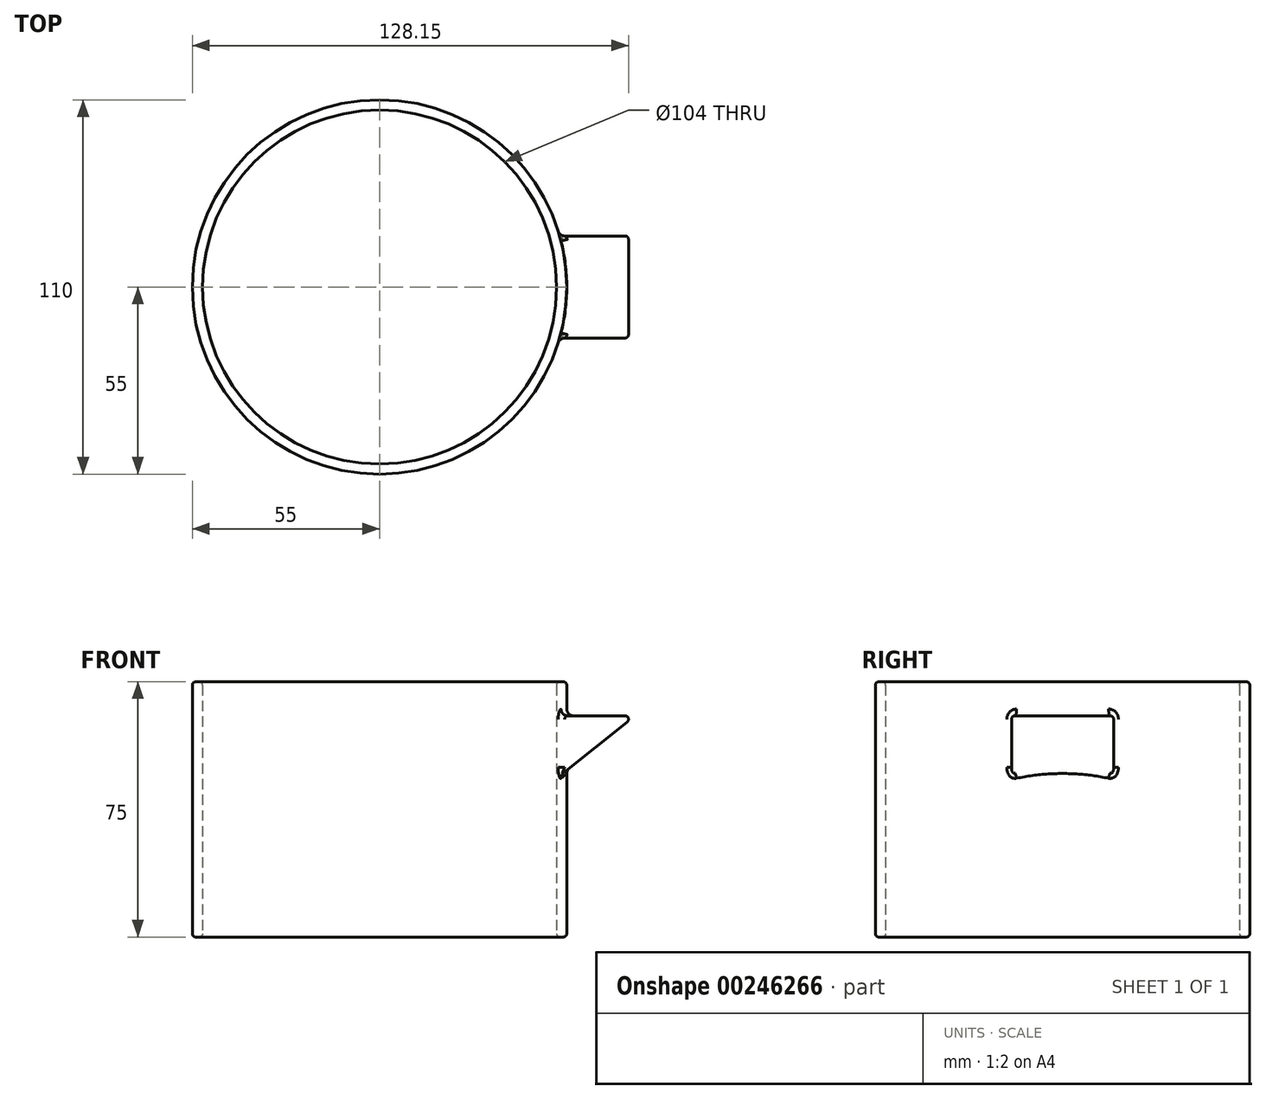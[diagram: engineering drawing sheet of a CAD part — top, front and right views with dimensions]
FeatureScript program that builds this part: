
annotation { "Feature Type Name" : "Feature", "Feature Type Description" : "" }
export const myFeature = defineFeature(function(context is Context, id is Id, definition is map)
    precondition{}
    {
        {
            var Q0;
            Q0=qCreatedBy(makeId("Top.planeOp"),FACE);
            var sketch = newSketch(context, id + "F0", { "sketchPlane" : qUnion([Q0])});
            skCircle(sketch, "E0", {"center": v(0, 0) * mm, "radius": 55 * mm});
            skCircle(sketch, "E1", {"center": v(0, 0) * mm, "radius": 52 * mm});
            skSolve(sketch);
        }
        {
            var Q0;
            Q0 = qSketchRegion(id + "F0", true);
            extrude(context, id + "F1", {"entities" : qUnion([Q0]), "depth" : 75 * mm});
        }
        {
            var Q0;
            Q0=qCreatedBy(makeId("Front.planeOp"),FACE);
            var sketch = newSketch(context, id + "F2", { "sketchPlane" : qUnion([Q0])});
            skLineSegment(sketch, "E2", {"start": v(50, 65) * mm, "end": v(75, 65) * mm});
            skLineSegment(sketch, "E3", {"start": v(75, 65) * mm, "end": v(50, 45) * mm});
            skLineSegment(sketch, "E4", {"start": v(50, 45) * mm, "end": v(50, 65) * mm});
            skSolve(sketch);
        }
        {
            var Q0;
            Q0 = qSketchRegion(id + "F2", true);
            extrude(context, id + "F3", {"entities" : qUnion([Q0]), "operationType" : NewBodyOperationType.ADD, "endBound" : BoundingType.SYMMETRIC, "depth" : 30 * mm});
        }
        {
            var Q0;
            Q0=makeQuery(id+"F1.opExtrude","CAP_FACE",FACE,{"disambiguationData":[OSD([sQuery(id+"F0.wireOp",EDGE,"E0"),sQuery(id+"F0.wireOp",EDGE,"E1")])],"isStart":false});
            var sketch = newSketch(context, id + "F4", { "sketchPlane" : qUnion([Q0])});
            skCircle(sketch, "E5.0", {"center": v(0, 0) * mm, "radius": 52 * mm});
            skSolve(sketch);
        }
        {
            var Q0;
            Q0 = qSketchRegion(id + "F4", true);
            extrude(context, id + "F5", {"entities" : qUnion([Q0]), "operationType" : NewBodyOperationType.REMOVE, "endBound" : BoundingType.THROUGH_ALL, "oppositeDirection" : true, "depth" : 25 * mm});
        }
        {
            var Q0;
            Q0=makeQuery(id+"F3.opExtrude","SWEPT_EDGE",EDGE,{"disambiguationData":[OSD([sQuery(id+"F2.wireOp",EDGE,"E2"),sQuery(id+"F2.wireOp",EDGE,"E3")])]});
            var Q1;
            Q1=makeQuery(id+"FyLVPSFapYQUoZB_1.1.F3.opExtrude","SWEPT_EDGE",EDGE,{"disambiguationData":[OSD([sQuery(id+"F2.wireOp",EDGE,"E2"),sQuery(id+"F2.wireOp",EDGE,"E3")])]});
            var Q2;
            Q2=makeQuery(id+"FyLVPSFapYQUoZB_1.1.F3.opExtrude","CAP_EDGE",EDGE,{"disambiguationData":[OSD([sQuery(id+"F2.wireOp",EDGE,"E3")])],"isStart":false});
            var Q3;
            Q3=makeQuery(id+"FyLVPSFapYQUoZB_1.1.F3.opExtrude","CAP_EDGE",EDGE,{"disambiguationData":[OSD([sQuery(id+"F2.wireOp",EDGE,"E2")])],"isStart":false});
            var Q4;
            Q4=makeQuery(id+"F3.opExtrude","CAP_EDGE",EDGE,{"disambiguationData":[OSD([sQuery(id+"F2.wireOp",EDGE,"E2")])],"isStart":false});
            var Q5;
            Q5=makeQuery(id+"F3.opExtrude","CAP_EDGE",EDGE,{"disambiguationData":[OSD([sQuery(id+"F2.wireOp",EDGE,"E3")])],"isStart":false});
            var Q6;
            Q6=makeQuery(id+"F3.opExtrude","CAP_EDGE",EDGE,{"disambiguationData":[OSD([sQuery(id+"F2.wireOp",EDGE,"E2")])],"isStart":true});
            var Q7;
            Q7=makeQuery(id+"F3.opExtrude","CAP_EDGE",EDGE,{"disambiguationData":[OSD([sQuery(id+"F2.wireOp",EDGE,"E3")])],"isStart":true});
            var Q8;
            Q8=makeQuery(id+"FyLVPSFapYQUoZB_1.1.F3.opExtrude","CAP_EDGE",EDGE,{"disambiguationData":[OSD([sQuery(id+"F2.wireOp",EDGE,"E3")])],"isStart":true});
            var Q9;
            Q9=makeQuery(id+"FyLVPSFapYQUoZB_1.1.F3.opExtrude","CAP_EDGE",EDGE,{"disambiguationData":[OSD([sQuery(id+"F2.wireOp",EDGE,"E2")])],"isStart":true});
            fillet(context, id + "F6", {"entities" : qUnion([Q0, Q1, Q2, Q3, Q4, Q5, Q6, Q7, Q8, Q9]), "radius" : 1 * mm, "tangentPropagation" : true, "allowEdgeOverflow" : false});
        }
        {
            var Q0;
            Q0=makeQuery(id+"F3.boolean.opBoolean","INTERSECT",EDGE,{"derivedFrom":[makeQuery(id+"F1.opExtrude","SWEPT_FACE",FACE,{"disambiguationData":[OSD([sQuery(id+"F0.wireOp",EDGE,"E0")])]}),makeQuery(id+"F3.opExtrude","SWEPT_FACE",FACE,{"disambiguationData":[OSD([sQuery(id+"F2.wireOp",EDGE,"E2")])]})]});
            var Q1;
            Q1=makeQuery(id+"FyLVPSFapYQUoZB_1.1.F3.boolean.opBoolean","INTERSECT",EDGE,{"derivedFrom":[makeQuery(id+"F1.opExtrude","SWEPT_FACE",FACE,{"disambiguationData":[OSD([sQuery(id+"F0.wireOp",EDGE,"E0")])]}),makeQuery(id+"FyLVPSFapYQUoZB_1.1.F3.opExtrude","SWEPT_FACE",FACE,{"disambiguationData":[OSD([sQuery(id+"F2.wireOp",EDGE,"E2")])]})]});
            fillet(context, id + "F7", {"entities" : qUnion([Q0, Q1]), "radius" : 2 * mm, "tangentPropagation" : true, "allowEdgeOverflow" : false});
        }
        {
            var Q0;
            Q0=makeQuery(id+"F1.opExtrude","CAP_EDGE",EDGE,{"disambiguationData":[OSD([sQuery(id+"F0.wireOp",EDGE,"E1")])],"isStart":false});
            var Q1;
            Q1=makeQuery(id+"F1.opExtrude","CAP_EDGE",EDGE,{"disambiguationData":[OSD([sQuery(id+"F0.wireOp",EDGE,"E0")])],"isStart":false});
            var Q2;
            Q2=makeQuery(id+"F1.opExtrude","CAP_EDGE",EDGE,{"disambiguationData":[OSD([sQuery(id+"F0.wireOp",EDGE,"E0")])],"isStart":true});
            var Q3;
            Q3=makeQuery(id+"F1.opExtrude","CAP_EDGE",EDGE,{"disambiguationData":[OSD([sQuery(id+"F0.wireOp",EDGE,"E1")])],"isStart":true});
            fillet(context, id + "F8", {"entities" : qUnion([Q0, Q1, Q2, Q3]), "radius" : 1 * mm, "tangentPropagation" : true, "allowEdgeOverflow" : false});
        }
    });
